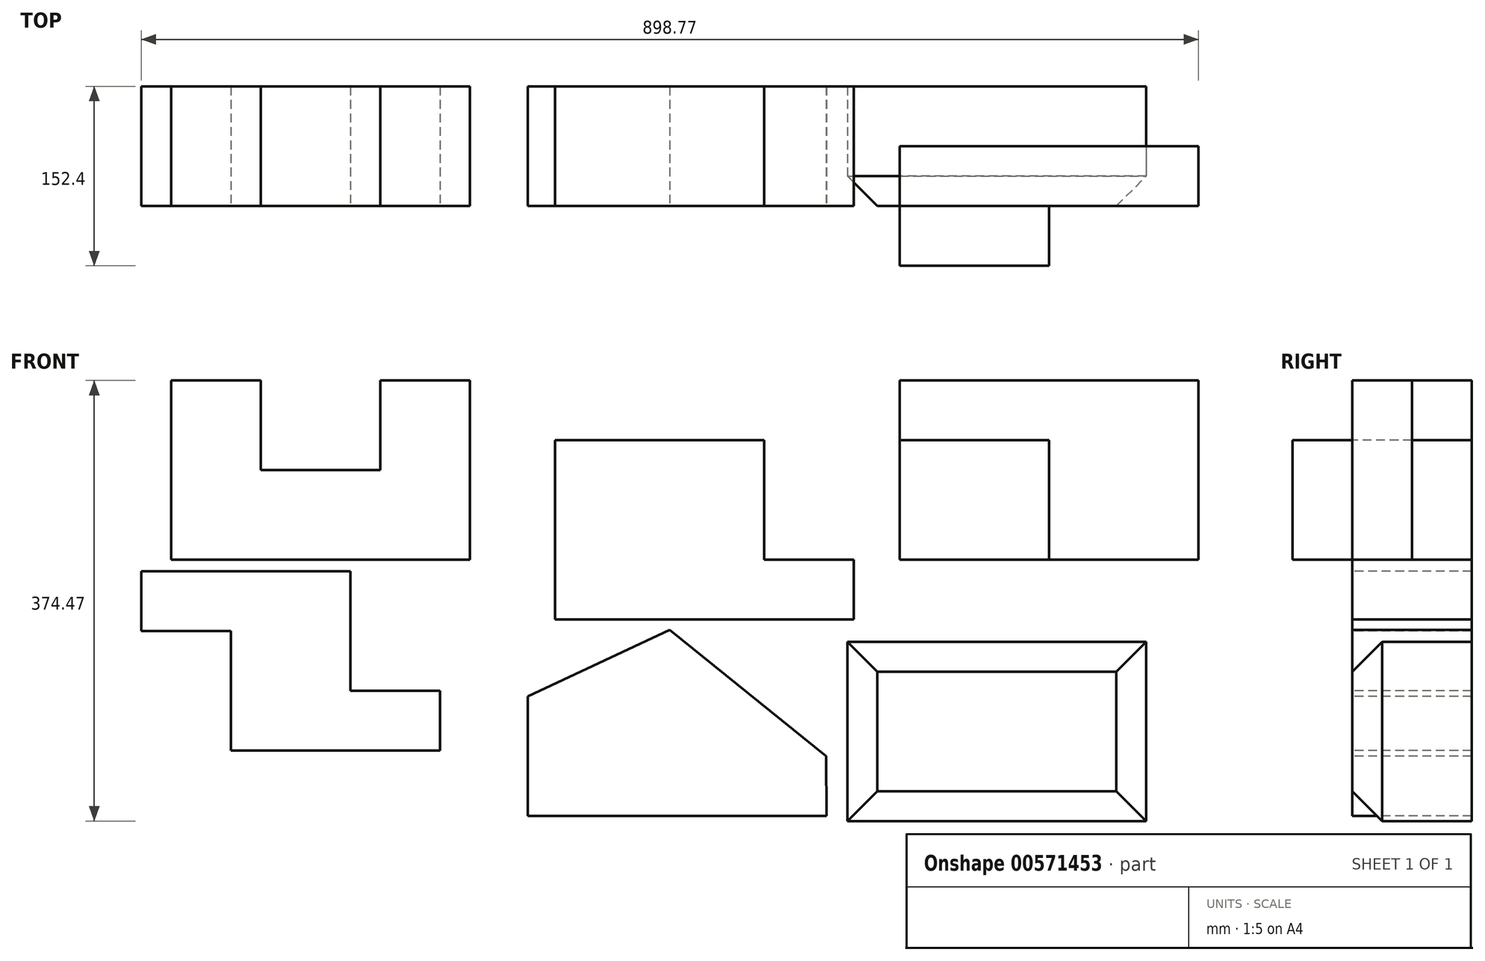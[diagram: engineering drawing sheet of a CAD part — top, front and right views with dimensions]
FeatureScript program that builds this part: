
annotation { "Feature Type Name" : "Feature", "Feature Type Description" : "" }
export const myFeature = defineFeature(function(context is Context, id is Id, definition is map)
    precondition{}
    {
        {
            var Q0;
            Q0=qCreatedBy(makeId("Front.planeOp"),FACE);
            var sketch = newSketch(context, id + "F0", { "sketchPlane" : qUnion([Q0])});
            skLineSegment(sketch, "E0", {"start": v(-183.5, 0) * mm, "end": v(0, 0) * mm});
            skLineSegment(sketch, "E1", {"start": v(-183.5, 0) * mm, "end": v(-183.5, 152.4) * mm});
            skLineSegment(sketch, "E2", {"start": v(-183.5, 152.4) * mm, "end": v(-259.7, 152.4) * mm});
            skLineSegment(sketch, "E3", {"start": v(-259.7, 152.4) * mm, "end": v(-259.7, 76.2) * mm});
            skLineSegment(sketch, "E4", {"start": v(-259.7, 76.2) * mm, "end": v(-361.3, 76.2) * mm});
            skLineSegment(sketch, "E5", {"start": v(-361.3, 76.2) * mm, "end": v(-361.3, 152.4) * mm});
            skLineSegment(sketch, "E6", {"start": v(-361.3, 152.4) * mm, "end": v(-437.5, 152.4) * mm});
            skLineSegment(sketch, "E7", {"start": v(-437.5, 152.4) * mm, "end": v(-437.5, 0) * mm});
            skLineSegment(sketch, "E8", {"start": v(-437.5, 0) * mm, "end": v(0, 0) * mm});
            skSolve(sketch);
        }
        {
            var Q0;
            Q0=qCreatedBy(makeId("Front.planeOp"),FACE);
            var sketch = newSketch(context, id + "F1", { "sketchPlane" : qUnion([Q0])});
            skLineSegment(sketch, "E9", {"start": v(181.78, 152.49) * mm, "end": v(181.78, 0.09) * mm});
            skLineSegment(sketch, "E10", {"start": v(181.78, 0.09) * mm, "end": v(435.78, 0.09) * mm});
            skLineSegment(sketch, "E11", {"start": v(435.78, 0.09) * mm, "end": v(435.78, 152.49) * mm});
            skLineSegment(sketch, "E12", {"start": v(435.78, 152.49) * mm, "end": v(181.78, 152.49) * mm});
            skLineSegment(sketch, "E13", {"start": v(181.78, 0.09) * mm, "end": v(181.78, 0) * mm});
            skSolve(sketch);
        }
        {
            var Q0;
            Q0 = qSketchRegion(id + "F0", true);
            extrude(context, id + "F2", {"entities" : qUnion([Q0]), "oppositeDirection" : true, "depth" : 101.6 * mm, "offsetDistance" : 25.4 * mm});
        }
        {
            var Q0;
            Q0 = qSketchRegion(id + "F1", true);
            extrude(context, id + "F3", {"entities" : qUnion([Q0]), "oppositeDirection" : true, "depth" : 50.8 * mm, "offsetDistance" : 25.4 * mm});
        }
        {
            var Q0;
            Q0=makeQuery(id+"F3.opExtrude","CAP_FACE",FACE,{"disambiguationData":[OSD([sQuery(id+"F1.wireOp",EDGE,"E9"),sQuery(id+"F1.wireOp",EDGE,"E10"),sQuery(id+"F1.wireOp",EDGE,"E11"),sQuery(id+"F1.wireOp",EDGE,"E12"),sQuery(id+"F1.wireOp",EDGE,"E13")])],"isStart":true});
            var sketch = newSketch(context, id + "F4", { "sketchPlane" : qUnion([Q0])});
            skLineSegment(sketch, "E14", {"start": v(181.78, 101.69) * mm, "end": v(308.78, 101.69) * mm});
            skLineSegment(sketch, "E15", {"start": v(308.78, 0.09) * mm, "end": v(181.78, 0.09) * mm});
            skLineSegment(sketch, "E16", {"start": v(181.78, 0.09) * mm, "end": v(181.78, 101.69) * mm});
            skLineSegment(sketch, "E17", {"start": v(308.78, 101.69) * mm, "end": v(308.78, 0.09) * mm});
            skSolve(sketch);
        }
        {
            var Q0;
            Q0=makeQuery(id+"F4.imprint","IMPRINT",FACE,{"disambiguationData":[TD([[makeQuery(id+"F4.imprint","IMPRINT",EDGE,{"derivedFrom":sQuery(id+"F4.wireOp",EDGE,"E14")}),-1.0]])]});
            extrude(context, id + "F5", {"entities" : qUnion([Q0]), "operationType" : NewBodyOperationType.ADD, "depth" : 50.8 * mm, "offsetDistance" : 25.4 * mm});
        }
        {
            var Q0;
            Q0=qCreatedBy(makeId("Front.planeOp"),FACE);
            var sketch = newSketch(context, id + "F6", { "sketchPlane" : qUnion([Q0])});
            skLineSegment(sketch, "E18", {"start": v(-111.1, 101.6) * mm, "end": v(66.7, 101.6) * mm});
            skLineSegment(sketch, "E19", {"start": v(66.7, 0) * mm, "end": v(66.7, 101.6) * mm});
            skLineSegment(sketch, "E20", {"start": v(66.7, 0) * mm, "end": v(142.9, 0) * mm});
            skLineSegment(sketch, "E21", {"start": v(142.9, 0) * mm, "end": v(142.9, -50.8) * mm});
            skLineSegment(sketch, "E22", {"start": v(142.9, -50.8) * mm, "end": v(-111.1, -50.8) * mm});
            skLineSegment(sketch, "E23", {"start": v(-111.1, -50.8) * mm, "end": v(-111.1, 101.6) * mm});
            skSolve(sketch);
        }
        {
            var Q0;
            Q0 = qSketchRegion(id + "F6", true);
            extrude(context, id + "F7", {"entities" : qUnion([Q0]), "oppositeDirection" : true, "depth" : 101.6 * mm, "offsetDistance" : 25.4 * mm});
        }
        {
            var Q0;
            Q0=makeQuery(id+"F7.opExtrude","CAP_FACE",FACE,{"disambiguationData":[OSD([sQuery(id+"F6.wireOp",EDGE,"E18"),sQuery(id+"F6.wireOp",EDGE,"E19"),sQuery(id+"F6.wireOp",EDGE,"E20"),sQuery(id+"F6.wireOp",EDGE,"E21"),sQuery(id+"F6.wireOp",EDGE,"E22"),sQuery(id+"F6.wireOp",EDGE,"E23")])],"isStart":true});
            var sketch = newSketch(context, id + "F8", { "sketchPlane" : qUnion([Q0])});
            skLineSegment(sketch, "E24", {"start": v(-462.99, -60.5) * mm, "end": v(-386.79, -60.5) * mm});
            skLineSegment(sketch, "E25", {"start": v(-386.79, -60.5) * mm, "end": v(-386.79, -162.1) * mm});
            skLineSegment(sketch, "E26", {"start": v(-386.79, -162.1) * mm, "end": v(-208.99, -162.1) * mm});
            skLineSegment(sketch, "E27", {"start": v(-208.99, -162.1) * mm, "end": v(-208.99, -111.3) * mm});
            skLineSegment(sketch, "E28", {"start": v(-208.99, -111.3) * mm, "end": v(-285.19, -111.3) * mm});
            skLineSegment(sketch, "E29", {"start": v(-285.19, -111.3) * mm, "end": v(-285.19, -9.7) * mm});
            skLineSegment(sketch, "E30", {"start": v(-462.99, -60.5) * mm, "end": v(-462.99, -9.7) * mm});
            skLineSegment(sketch, "E31", {"start": v(-462.99, -9.7) * mm, "end": v(-285.19, -9.7) * mm});
            skSolve(sketch);
        }
        {
            var Q0;
            Q0 = qSketchRegion(id + "F8", true);
            extrude(context, id + "F9", {"entities" : qUnion([Q0]), "oppositeDirection" : true, "depth" : 101.6 * mm, "offsetDistance" : 25.4 * mm});
        }
        {
            var Q0;
            Q0=qCreatedBy(makeId("Front.planeOp"),FACE);
            var sketch = newSketch(context, id + "F10", { "sketchPlane" : qUnion([Q0])});
            skLineSegment(sketch, "E32", {"start": v(-134.53, -217.74) * mm, "end": v(119.47, -217.74) * mm});
            skLineSegment(sketch, "E33", {"start": v(-13.72, -59.47) * mm, "end": v(-134.53, -116.14) * mm});
            skLineSegment(sketch, "E34", {"start": v(-13.72, -59.47) * mm, "end": v(119.36, -166.94) * mm});
            skLineSegment(sketch, "E35", {"start": v(-134.53, -116.14) * mm, "end": v(-134.53, -217.74) * mm});
            skLineSegment(sketch, "E36", {"start": v(119.36, -166.94) * mm, "end": v(119.47, -217.74) * mm});
            skSolve(sketch);
        }
        {
            var Q0;
            Q0 = qSketchRegion(id + "F10", true);
            extrude(context, id + "F11", {"entities" : qUnion([Q0]), "oppositeDirection" : true, "depth" : 101.6 * mm, "offsetDistance" : 25.4 * mm});
        }
        {
            var Q0;
            Q0=qCreatedBy(makeId("Front.planeOp"),FACE);
            var sketch = newSketch(context, id + "F12", { "sketchPlane" : qUnion([Q0])});
            skLineSegment(sketch, "E37", {"start": v(137.47, -69.58) * mm, "end": v(137.47, -221.98) * mm});
            skLineSegment(sketch, "E38", {"start": v(137.47, -221.98) * mm, "end": v(391.47, -221.98) * mm});
            skLineSegment(sketch, "E39", {"start": v(391.47, -221.98) * mm, "end": v(391.47, -69.58) * mm});
            skLineSegment(sketch, "E40", {"start": v(137.47, -69.58) * mm, "end": v(391.47, -69.58) * mm});
            skSolve(sketch);
        }
        {
            var Q0;
            Q0 = qSketchRegion(id + "F12", true);
            extrude(context, id + "F13", {"entities" : qUnion([Q0]), "oppositeDirection" : true, "depth" : 101.6 * mm, "offsetDistance" : 25.4 * mm});
        }
        {
            var Q0;
            Q0=makeQuery(id+"F13.opExtrude","CAP_FACE",FACE,{"disambiguationData":[OSD([sQuery(id+"F12.wireOp",EDGE,"E37"),sQuery(id+"F12.wireOp",EDGE,"E38"),sQuery(id+"F12.wireOp",EDGE,"E39"),sQuery(id+"F12.wireOp",EDGE,"E40")])],"isStart":true});
            chamfer(context, id + "F14", {"entities" : qUnion([Q0]), "width" : 25.4 * mm, "tangentPropagation" : true});
        }
    });
